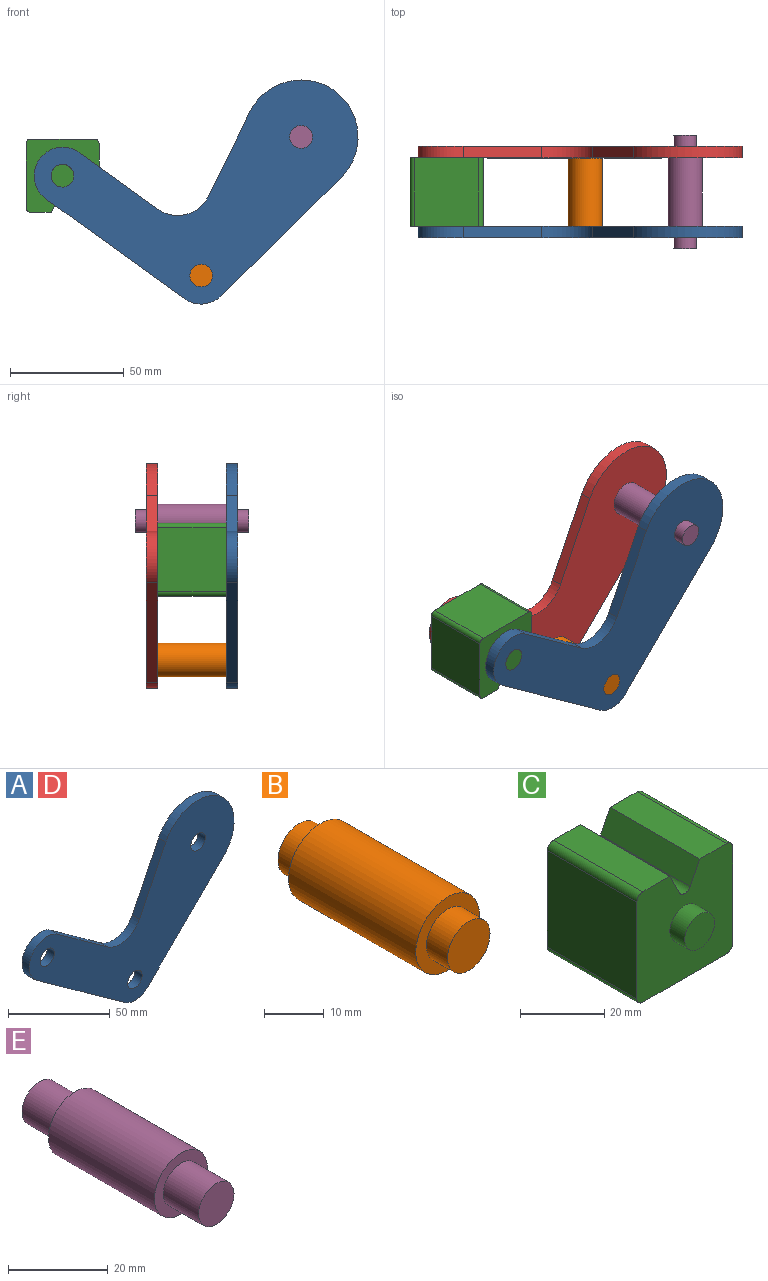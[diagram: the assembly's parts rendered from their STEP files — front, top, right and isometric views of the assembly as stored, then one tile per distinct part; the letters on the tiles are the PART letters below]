
ASSEMBLY  parts=5 mates=4
PART A: 13 faces, bbox 142.2x5x98.4 mm
  f0: plane 52.61x51.97mm, normal (0.7,0,-0.71), area 369.8mm2, adj f1,f9,f11,f12
  f1: cylinder r=25mm len=47.44mm, axis (0,-1,0), area 434.6mm2, adj f0,f2,f11,f12
  f2: plane 37.17x18.26mm, normal (-0.9,0,0.44), area 207.1mm2, adj f1,f3,f11,f12
  f3: cylinder r=15mm len=22.23mm, axis (0,-1,0), area 130.4mm2, adj f2,f4,f11,f12
  f4: plane 34.46x24.81mm, normal (0.58,0,0.81), area 212.3mm2, adj f3,f5,f11,f12
  f5: cylinder r=12.5mm len=22.64mm, axis (0,-1,0), area 196.3mm2, adj f4,f6,f11,f12
  f6: plane 60.86x43.82mm, normal (-0.58,0,-0.81), area 375mm2, adj f5,f9,f11,f12
  f7: cylinder r=5mm len=10mm, axis (0,-1,0), area 157.1mm2, adj f11,f12
  f8: cylinder r=5mm len=10mm, axis (0,-1,0), area 157.1mm2, adj f11,f12
  f9: cylinder r=12.5mm len=16.09mm, axis (0,-1,0), area 87.7mm2, adj f0,f6,f11,f12
  f10: cylinder r=5mm len=10mm, axis (0,-1,0), area 157.1mm2, adj f11,f12
  f11: plane 142.19x98.36mm, normal (0,1,0), area 5739.8mm2, adj f0,f1,f2,f3,f4,f5,f6,f7
  f12: plane 142.19x98.36mm, normal (0,-1,0), area 5739.8mm2, adj f0,f1,f2,f3,f4,f5,f6,f7
PART B: 7 faces, bbox 15x40x15 mm
  f0: cylinder r=7.5mm len=30mm, axis (0,-1,0), area 1413.7mm2, adj f2,f5
  f1: cylinder r=5mm len=10mm, axis (0,-1,0), area 157.1mm2, adj f2,f3
  f2: plane 15x15mm, normal (0,-1,0), area 98.2mm2, adj f0,f1
  f3: plane 10x10mm, normal (0,-1,0), area 78.5mm2, adj f1
  f4: cylinder r=5mm len=10mm, axis (0,1,0), area 157.1mm2, adj f5,f6
  f5: plane 15x15mm, normal (0,1,0), area 98.2mm2, adj f0,f4
  f6: plane 10x10mm, normal (0,1,0), area 78.5mm2, adj f4
PART C: 18 faces, bbox 32.1x40x32.1 mm
  f0: plane 30x6.42mm, normal (0.89,0,0.45), area 215.4mm2, adj f4,f6,f10,f13
  f1: plane 30x6.42mm, normal (-0.89,0,0.45), area 215.4mm2, adj f2,f4,f10,f13
  f2: plane 30x9.04mm, normal (0,0,1), area 271.2mm2, adj f1,f4,f10,f14
  f3: plane 30x28.08mm, normal (1,0,0), area 842.3mm2, adj f4,f10,f14,f15
  f4: plane 32.08x32.08mm, normal (0,-1,0), area 900.6mm2, adj f0,f1,f2,f3,f5,f6,f7,f9
  f5: plane 30x28.08mm, normal (0,0,-1), area 842.3mm2, adj f4,f10,f15,f16
  f6: plane 30x9.04mm, normal (0,0,1), area 271.2mm2, adj f0,f4,f10,f17
  f7: plane 30x28.08mm, normal (-1,0,0), area 842.3mm2, adj f4,f10,f16,f17
  f8: plane 10x10mm, normal (0,-1,0), area 78.5mm2, adj f9
  f9: cylinder r=5mm len=10mm, axis (0,1,0), area 157.1mm2, adj f4,f8
  f10: plane 32.08x32.08mm, normal (0,1,0), area 900.6mm2, adj f0,f1,f2,f3,f5,f6,f7,f12
  f11: plane 10x10mm, normal (0,1,0), area 78.5mm2, adj f12
  f12: cylinder r=5mm len=10mm, axis (0,-1,0), area 157.1mm2, adj f10,f11
  f13: cylinder r=2mm len=30mm, axis (0,1,0), area 132.9mm2, adj f0,f1,f4,f10
  f14: cylinder r=2mm len=30mm, axis (0,1,0), area 94.2mm2, adj f2,f3,f4,f10
  f15: cylinder r=2mm len=30mm, axis (0,-1,0), area 94.2mm2, adj f3,f4,f5,f10
  f16: cylinder r=2mm len=30mm, axis (0,1,0), area 94.2mm2, adj f4,f5,f7,f10
  f17: cylinder r=2mm len=30mm, axis (0,-1,0), area 94.2mm2, adj f4,f6,f7,f10
PART D: same geometry as A
PART E: 7 faces, bbox 15x50x15 mm
  f0: cylinder r=7.5mm len=30mm, axis (0,-1,0), area 1413.7mm2, adj f2,f5
  f1: cylinder r=5mm len=10mm, axis (0,1,0), area 314.2mm2, adj f2,f3
  f2: plane 15x15mm, normal (0,-1,0), area 98.2mm2, adj f0,f1
  f3: plane 10x10mm, normal (0,-1,0), area 78.5mm2, adj f1
  f4: cylinder r=5mm len=10mm, axis (0,-1,0), area 314.2mm2, adj f5,f6
  f5: plane 15x15mm, normal (0,1,0), area 98.2mm2, adj f0,f4
  f6: plane 10x10mm, normal (0,1,0), area 78.5mm2, adj f4
PLACE A t=(0,-20,0)mm
PLACE B t=(0,-20,0)mm
PLACE C rot(axis=(1,0,0),180deg) t=(0,20,-34.08)mm
PLACE D t=(0,15,0)mm
PLACE E t=(0,-20,0)mm fixed
MATE revolute C.f9 <-> A.f5  axis (0,1,0) through (-104.69,-15,-17.04)mm
MATE fastened B.f0 <-> A.f7  axis (0,-1,0) through (-43.82,-15,-60.86)mm
MATE fastened E.f0 <-> A.f1  axis (0,-1,0) through (0,-15,0)mm
MATE fastened D.f1 <-> E.f0  axis (0,-1,0) through (0,15,0)mm
